# Revit family: Sink-Kitchen-KOHLER-Vault-K-3942
name_source: partatom
category: Plumbing Fixtures
revit_build: Autodesk Revit 2015 (Build: 20140606_1530(x64)
units: mm (PartAtom-declared; Revit-internal decimal feet)

## types (3) — shared parameters
ADA Compliant = No
Assembly Code = D2010400
CW Connection = No
Cold Water Inlet = Cold Water Inlet
Date Modified = 04/24/2019
Default Elevation = 36"
Description = 35-3/4 inch x 24-5/16 inch x 9-5/16 inch Self-Trimming top-mount single-bowl stainless steel apron-front kitchen sink for 36 inch Cabinet
Drain Included = No
Finish = Kohler-Metal-NA-Stainless
HW Connection = No
Height = 9 5/16"
Hot Water Inlet = Hot Water Inlet
Length = 35 3/4"
Manufacturer = KOHLER Co.
MasterFormat 1995 = 15410
MasterFormat 2004 = 22.41.16
Material = 18 Gauge Stainless Steel
Product Documentation Link = https://www.us.kohler.com
Product Name = Vault
Product Page URL = http://www.us.kohler.com
URL = https://www.us.kohler.com
Vent Connection = No
Waste Connection = Yes
Waste Water Outlet = Waste Water Outlet
WaterSense Certified = No
Width = 24 5/16"

## per-type parameters (varying)
| type | Faucet Hole Distance | Four Hole Sink | Fourth Hole Distance | Model | Single Hole Sink | Three Hole Sink | Type |
| Single Hole Sink, NA-Stainless Steel | 0" | No | 0" | K-3942-1-NA | Yes | No | 1 |
| Three Hole Sink, NA-Stainless Steel | 8" | No | 0" | K-3942-3-NA | No | Yes | 2 |
| Four Hole Sink, NA-Stainless Steel | 8" | Yes | 9 1/8" | K-3942-4-NA | No | No | 3 |

## geometry (parser evidence)
native form markers: Sweep x6
no freeform markers — native parametric forms only
